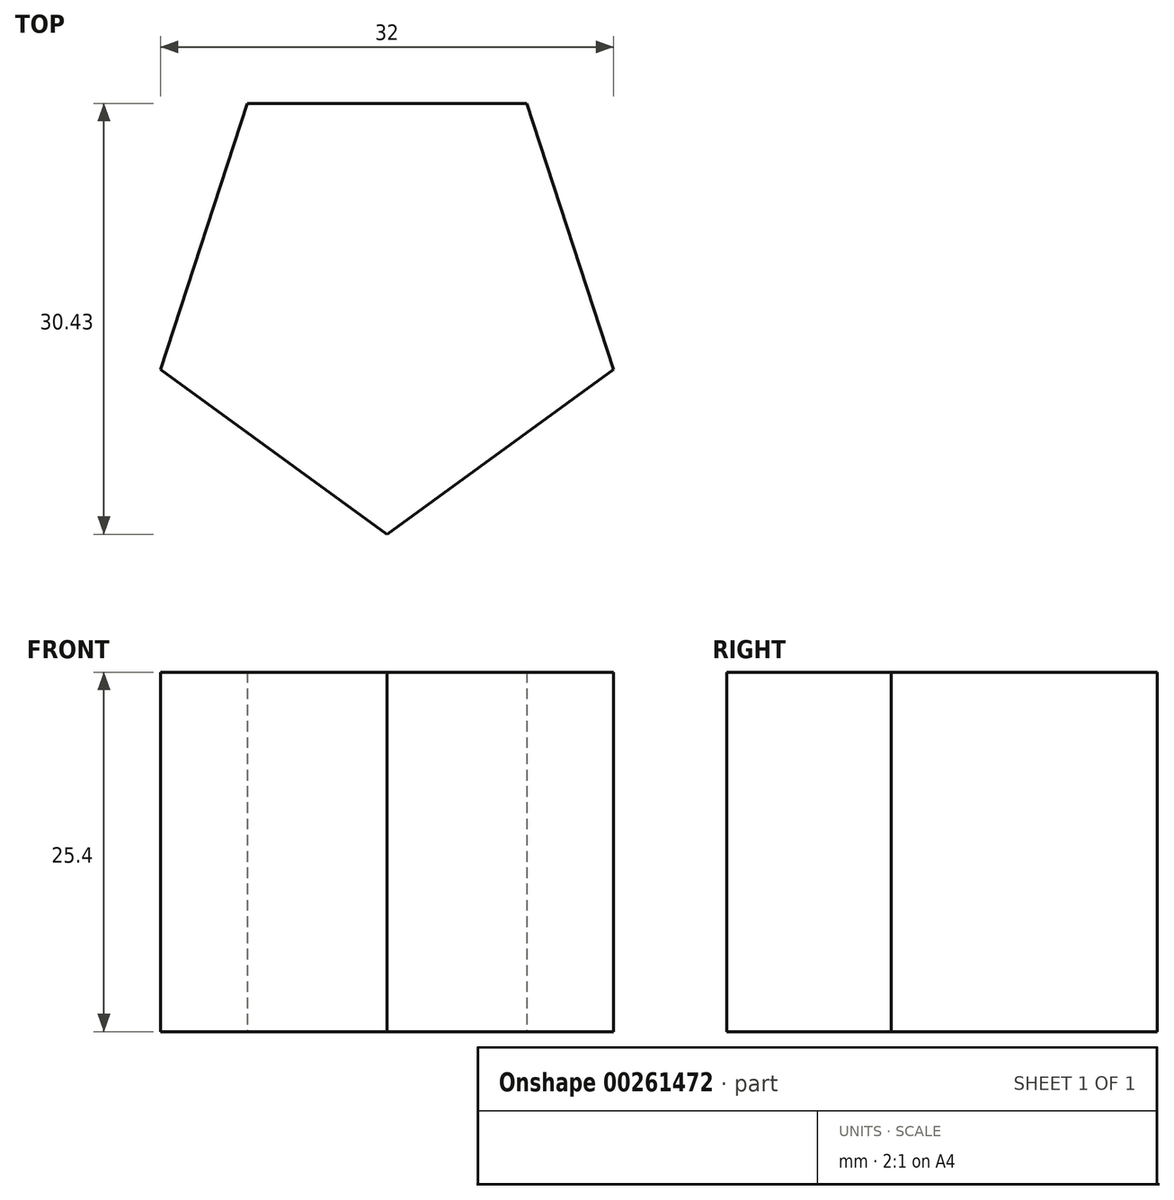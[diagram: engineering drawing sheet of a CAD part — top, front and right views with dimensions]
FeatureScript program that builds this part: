
annotation { "Feature Type Name" : "Feature", "Feature Type Description" : "" }
export const myFeature = defineFeature(function(context is Context, id is Id, definition is map)
    precondition{}
    {
        {
            var Q0;
            Q0=qCreatedBy(makeId("Top.planeOp"),FACE);
            var sketch = newSketch(context, id + "F0", { "sketchPlane" : qUnion([Q0])});
            skCircle(sketch, "E0.cCircle", {"center": v(0, 0) * mm, "radius": 13.6 * mm, "construction": true});
            skLineSegment(sketch, "E0.0", {"start": v(-9.89, 13.6) * mm, "end": v(9.89, 13.6) * mm});
            skLineSegment(sketch, "E0.1", {"start": v(9.89, 13.6) * mm, "end": v(16, -5.2) * mm});
            skLineSegment(sketch, "E0.2", {"start": v(16, -5.2) * mm, "end": v(0, -16.82) * mm});
            skLineSegment(sketch, "E0.3", {"start": v(0, -16.82) * mm, "end": v(-16, -5.2) * mm});
            skLineSegment(sketch, "E0.4", {"start": v(-16, -5.2) * mm, "end": v(-9.89, 13.6) * mm});
            skPoint(sketch, "E0.0.midPoint", {"position": v(0, 13.6) * mm});
            skSolve(sketch);
        }
        {
            var Q0;
            Q0 = qSketchRegion(id + "F0", true);
            extrude(context, id + "F1", {"entities" : qUnion([Q0]), "depth" : 25.4 * mm});
        }
    });
